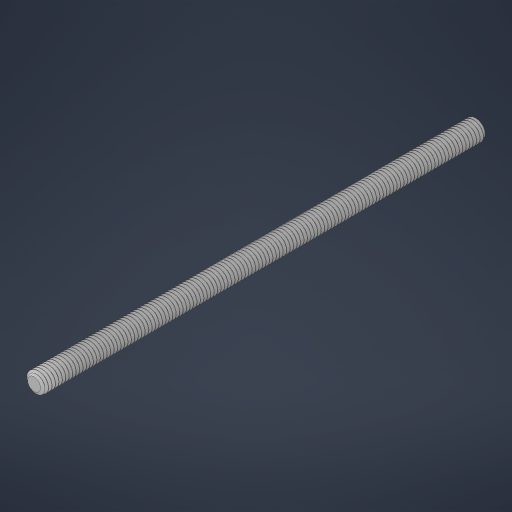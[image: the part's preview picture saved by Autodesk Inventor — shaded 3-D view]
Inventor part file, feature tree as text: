
AUTODESK INVENTOR PART (.ipt)
format: ipt  version: 2023 (Build 270158000, 158)  size: 3,208,192 bytes
history: native  units: in
note: dims shown in document units (in); Inventor stores cm internally (conversion verified against a paired STEP export)
features: mirror x1
ambient origin geometry x8: Origin, YZ Plane, XZ Plane, XY Plane, X Axis, Y Axis, Z Axis, Center Point
bodies: Solid1 (feature_tree)
feature tree (1):
  mirror  "Mirror1"
